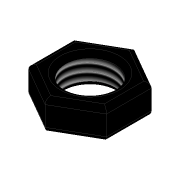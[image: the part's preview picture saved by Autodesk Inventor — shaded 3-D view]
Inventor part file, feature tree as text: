
AUTODESK INVENTOR PART (.ipt)
format: ipt  version: 2020 (Build 240168000, 168)  size: 136,704 bytes
history: native  units: mm
features: extrude x1, fillet x1, thread x1, sketch x1
ambient origin geometry x8: Origin, YZ Plane, XZ Plane, XY Plane, X Axis, Y Axis, Z Axis, Center Point
bodies: Solid1 (feature_tree)
feature tree (4):
  extrude  "Extrusion1"  Depth=0.5mm
  fillet  "Fillet1"  Radius=3.0mm
  thread  "Thread1"  [1 undecoded]
  sketch  "Sketch1"  dims[d0=3.95mm d1=5.0mm d2=3.0mm d3=0.0mm d4=0.5mm d5=2.0mm d6=0.0mm]
note: 1 required parameter value undecoded (feature->parameter linkage not recoverable at this tier; creation-order binding heuristic only, values carry confidence <= 0.55)
